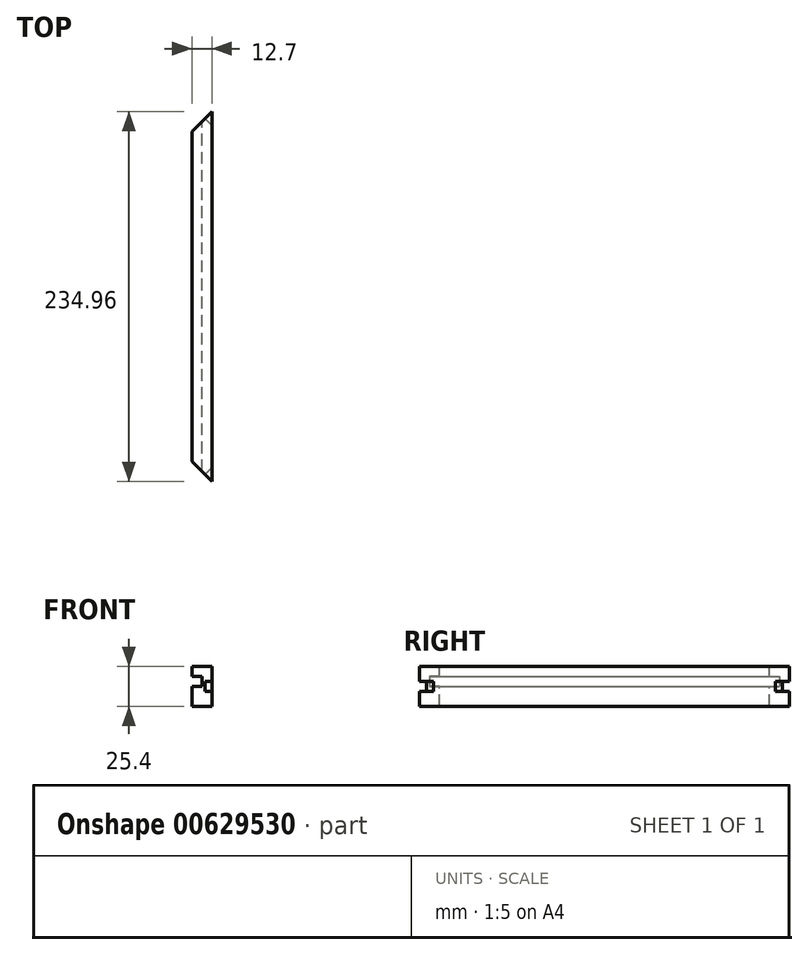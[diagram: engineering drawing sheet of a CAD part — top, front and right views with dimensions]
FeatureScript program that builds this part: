
annotation { "Feature Type Name" : "Feature", "Feature Type Description" : "" }
export const myFeature = defineFeature(function(context is Context, id is Id, definition is map)
    precondition{}
    {
        {
            var Q0;
            Q0=qCreatedBy(makeId("Right.planeOp"),FACE);
            var sketch = newSketch(context, id + "F0", { "sketchPlane" : qUnion([Q0])});
            skLineSegment(sketch, "E0.bottom", {"start": v(-117.48, 0) * mm, "end": v(117.47, 0) * mm});
            skLineSegment(sketch, "E0.top", {"start": v(-117.48, 25.4) * mm, "end": v(117.47, 25.4) * mm});
            skLineSegment(sketch, "E0.left", {"start": v(-117.48, 0) * mm, "end": v(-117.48, 25.4) * mm});
            skLineSegment(sketch, "E0.right", {"start": v(117.47, 0) * mm, "end": v(117.47, 25.4) * mm});
            skSolve(sketch);
        }
        {
            var Q0;
            Q0=makeQuery(id+"F0.imprint","IMPRINT",FACE,{"disambiguationData":[TD([[makeQuery(id+"F0.imprint","IMPRINT",EDGE,{"derivedFrom":sQuery(id+"F0.wireOp",EDGE,"E0.bottom")}),1.0]])]});
            extrude(context, id + "F1", {"entities" : qUnion([Q0]), "depth" : 12.7 * mm, "offsetDistance" : 25.4 * mm});
        }
        {
            var Q0;
            Q0=makeQuery(id+"F1.opExtrude","SWEPT_FACE",FACE,{"disambiguationData":[OSD([sQuery(id+"F0.wireOp",EDGE,"E0.right")])]});
            var sketch = newSketch(context, id + "F2", { "sketchPlane" : qUnion([Q0])});
            skLineSegment(sketch, "E1.bottom", {"start": v(0, 19.05) * mm, "end": v(-6.35, 19.05) * mm});
            skLineSegment(sketch, "E1.top", {"start": v(0, 12.7) * mm, "end": v(-6.35, 12.7) * mm});
            skLineSegment(sketch, "E1.left", {"start": v(0, 19.05) * mm, "end": v(0, 12.7) * mm});
            skLineSegment(sketch, "E1.right", {"start": v(-6.35, 19.05) * mm, "end": v(-6.35, 12.7) * mm});
            skSolve(sketch);
        }
        {
            var Q0;
            Q0 = qSketchRegion(id + "F2", true);
            extrude(context, id + "F3", {"entities" : qUnion([Q0]), "operationType" : NewBodyOperationType.REMOVE, "endBound" : BoundingType.THROUGH_ALL, "oppositeDirection" : true, "depth" : 25.4 * mm, "offsetDistance" : 25.4 * mm});
        }
        {
            var Q0;
            Q0=makeQuery(id+"F1.opExtrude","SWEPT_FACE",FACE,{"disambiguationData":[OSD([sQuery(id+"F0.wireOp",EDGE,"E0.top")])]});
            var sketch = newSketch(context, id + "F4", { "sketchPlane" : qUnion([Q0])});
            skLineSegment(sketch, "E2", {"start": v(0, 104.77) * mm, "end": v(12.7, 117.47) * mm});
            skLineSegment(sketch, "E3", {"start": v(12.7, 117.47) * mm, "end": v(0, 117.47) * mm});
            skLineSegment(sketch, "E4", {"start": v(0, 117.47) * mm, "end": v(0, 104.77) * mm});
            skLineSegment(sketch, "E5.MirrorCS", {"start": v(0, -104.77) * mm, "end": v(12.7, -117.47) * mm});
            skLineSegment(sketch, "E6.MirrorCS", {"start": v(0, -117.47) * mm, "end": v(0, -104.77) * mm});
            skLineSegment(sketch, "E7.MirrorCS", {"start": v(12.7, -117.47) * mm, "end": v(0, -117.47) * mm});
            skSolve(sketch);
        }
        {
            var Q0;
            Q0 = qSketchRegion(id + "F4", true);
            extrude(context, id + "F5", {"entities" : qUnion([Q0]), "operationType" : NewBodyOperationType.REMOVE, "endBound" : BoundingType.THROUGH_ALL, "oppositeDirection" : true, "depth" : 25.4 * mm, "offsetDistance" : 25.4 * mm});
        }
        {
            var Q0;
            Q0=makeQuery(id+"F5.boolean.opBoolean","COPY",FACE,{"derivedFrom":makeQuery(id+"F5.opExtrude","SWEPT_FACE",FACE,{"disambiguationData":[OSD([sQuery(id+"F4.wireOp",EDGE,"E5.MirrorCS")])]})});
            var sketch = newSketch(context, id + "F6", { "sketchPlane" : qUnion([Q0])});
            skLineSegment(sketch, "E8.bottom", {"start": v(92.05, 15.88) * mm, "end": v(85.7, 15.88) * mm});
            skLineSegment(sketch, "E8.top", {"start": v(92.05, 9.52) * mm, "end": v(85.7, 9.52) * mm});
            skLineSegment(sketch, "E8.left", {"start": v(92.05, 15.88) * mm, "end": v(92.05, 9.52) * mm});
            skLineSegment(sketch, "E8.right", {"start": v(85.7, 15.88) * mm, "end": v(85.7, 9.52) * mm});
            skSolve(sketch);
        }
        {
            var Q0;
            Q0 = qSketchRegion(id + "F6", true);
            extrude(context, id + "F7", {"entities" : qUnion([Q0]), "operationType" : NewBodyOperationType.REMOVE, "endBound" : BoundingType.THROUGH_ALL, "oppositeDirection" : true, "depth" : 25.4 * mm, "offsetDistance" : 25.4 * mm});
        }
        {
            var Q0;
            Q0=makeQuery(id+"F5.boolean.opBoolean","COPY",FACE,{"derivedFrom":makeQuery(id+"F5.opExtrude","SWEPT_FACE",FACE,{"disambiguationData":[OSD([sQuery(id+"F4.wireOp",EDGE,"E2")])]})});
            var sketch = newSketch(context, id + "F8", { "sketchPlane" : qUnion([Q0])});
            skLineSegment(sketch, "E9.bottom", {"start": v(-92.05, 15.88) * mm, "end": v(-85.7, 15.88) * mm});
            skLineSegment(sketch, "E9.top", {"start": v(-92.05, 9.52) * mm, "end": v(-85.7, 9.52) * mm});
            skLineSegment(sketch, "E9.left", {"start": v(-92.05, 15.88) * mm, "end": v(-92.05, 9.53) * mm});
            skLineSegment(sketch, "E9.right", {"start": v(-85.7, 15.88) * mm, "end": v(-85.7, 9.53) * mm});
            skSolve(sketch);
        }
        {
            var Q0;
            Q0 = qSketchRegion(id + "F8", true);
            extrude(context, id + "F9", {"entities" : qUnion([Q0]), "operationType" : NewBodyOperationType.REMOVE, "endBound" : BoundingType.THROUGH_ALL, "oppositeDirection" : true, "depth" : 25.4 * mm, "offsetDistance" : 25.4 * mm});
        }
    });
